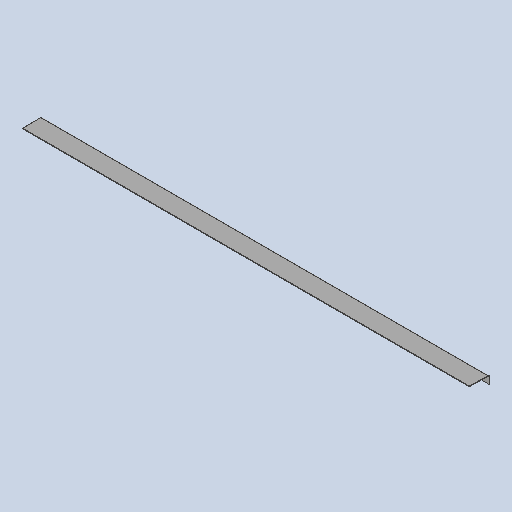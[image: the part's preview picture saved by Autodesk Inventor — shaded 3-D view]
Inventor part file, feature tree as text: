
AUTODESK INVENTOR PART (.ipt)
format: ipt  version: 2025 (Build 290162010, 162A)  size: 160,768 bytes
history: native  units: mm
features: sheet_metal_op x4, other x4, sketch x2, mirror x1
ambient origin geometry x8: Origin, YZ Plane, XZ Plane, XY Plane, X Axis, Y Axis, Z Axis, Center Point
bodies: Body1 (feature_tree)
feature tree (11):
  sheet_metal_op  "Face2"
  sheet_metal_op  "Flange3"
  other  "Corner Chamfer2"
  mirror  "Mirror1"
  sketch  "Sketch5"  dims[d26=1200.0mm]
  other  "Plate4"
  sketch  "Sketch6"  dims[d27=2897.0mm d28=3.0mm d29=53.0mm d30=947.0mm d31=150.0mm d32=103.0mm d36=100.0mm d37=100.0mm d38=100.0mm d39=850.0mm d40=1200.0mm d41=873.5mm d42=3.0mm d43=1.5mm d44=6.0mm d45=5.0mm d46=40.0mm d47=90.0deg d48=5.0mm d49=12.0mm d50=3.0mm d51=5.0mm d52=6.0mm d53=6.0mm d54=45.0deg]
  other  "Plate5"
  sheet_metal_op  "Bend3"
  sheet_metal_op  "Corner3"
  other  "Definition1"
